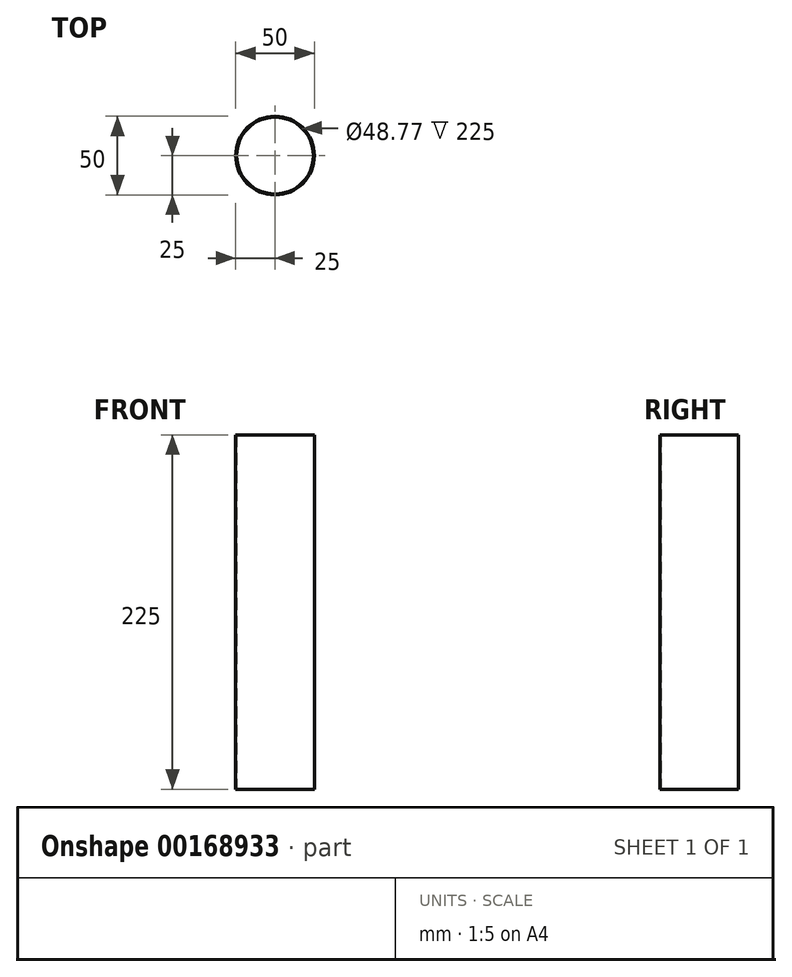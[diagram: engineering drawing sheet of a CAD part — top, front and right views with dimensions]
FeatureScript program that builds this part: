
annotation { "Feature Type Name" : "Feature", "Feature Type Description" : "" }
export const myFeature = defineFeature(function(context is Context, id is Id, definition is map)
    precondition{}
    {
        {
            var Q0;
            Q0=qCreatedBy(makeId("Top.planeOp"),FACE);
            var sketch = newSketch(context, id + "F0", { "sketchPlane" : qUnion([Q0])});
            skCircle(sketch, "E0", {"center": v(0, 0) * mm, "radius": 25 * mm});
            skCircle(sketch, "E1", {"center": v(0, 0) * mm, "radius": 24.38 * mm});
            skSolve(sketch);
        }
        {
            var Q0;
            Q0=makeQuery(id+"F0.imprint","IMPRINT",FACE,{"disambiguationData":[TD([[makeQuery(id+"F0.imprint","IMPRINT",EDGE,{"derivedFrom":sQuery(id+"F0.wireOp",EDGE,"E0")}),1.0]])]});
            extrude(context, id + "F1", {"entities" : qUnion([Q0]), "depth" : 225 * mm});
        }
    });
